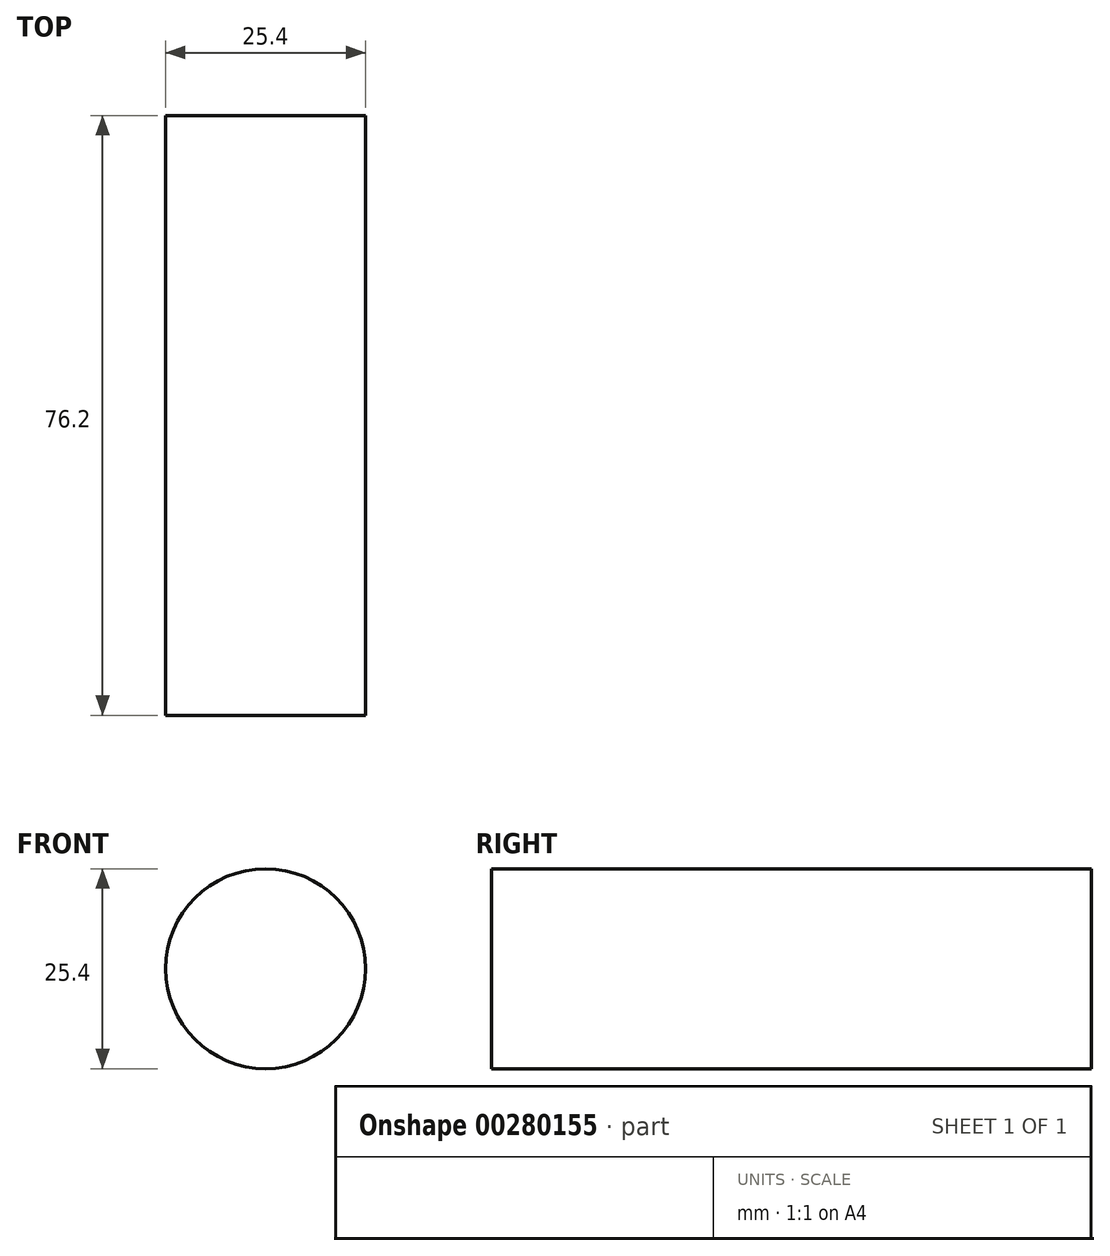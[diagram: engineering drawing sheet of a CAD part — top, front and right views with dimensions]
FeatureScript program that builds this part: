
annotation { "Feature Type Name" : "Feature", "Feature Type Description" : "" }
export const myFeature = defineFeature(function(context is Context, id is Id, definition is map)
    precondition{}
    {
        {
            var Q0;
            Q0=qCreatedBy(makeId("Front.planeOp"),FACE);
            var sketch = newSketch(context, id + "F0", { "sketchPlane" : qUnion([Q0])});
            skCircle(sketch, "E0", {"center": v(-45.38, 34.63) * mm, "radius": 12.7 * mm});
            skSolve(sketch);
        }
        {
            var Q0;
            Q0 = qSketchRegion(id + "F0", true);
            extrude(context, id + "F1", {"entities" : qUnion([Q0]), "depth" : 76.2 * mm});
        }
    });
